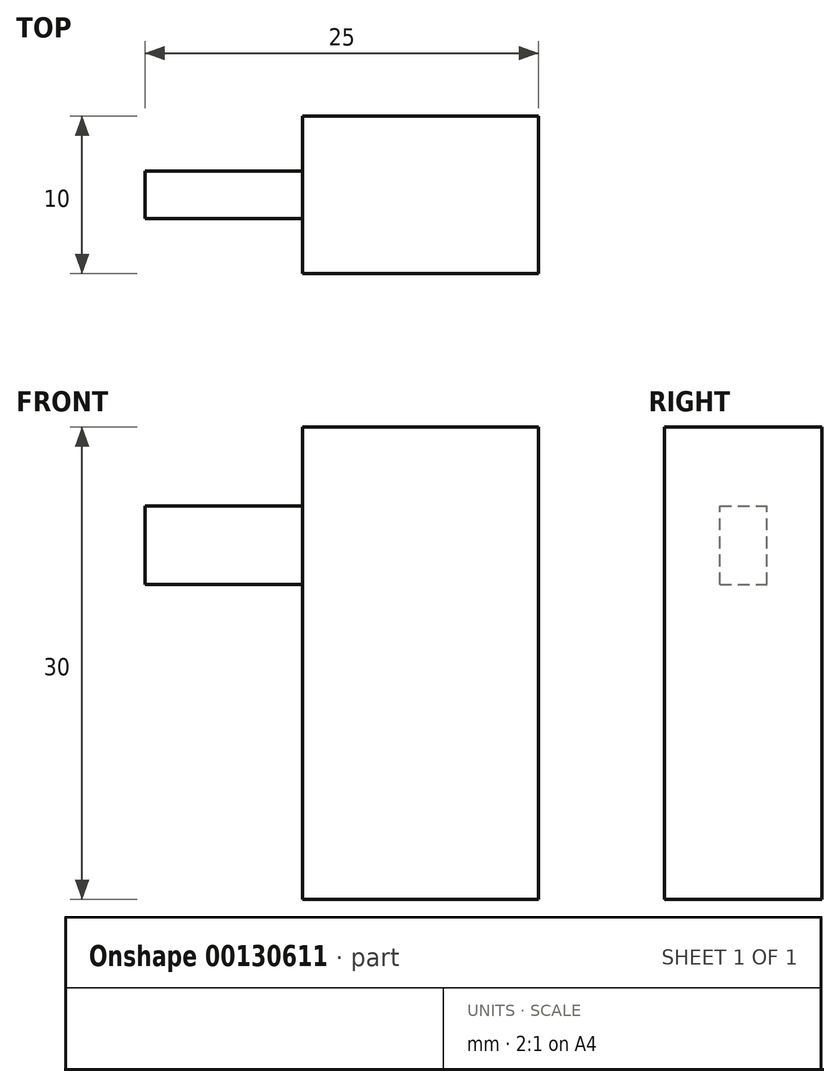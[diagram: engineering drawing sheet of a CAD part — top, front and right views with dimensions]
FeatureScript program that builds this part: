
annotation { "Feature Type Name" : "Feature", "Feature Type Description" : "" }
export const myFeature = defineFeature(function(context is Context, id is Id, definition is map)
    precondition{}
    {
        {
            var Q0;
            Q0=qCreatedBy(makeId("Front.planeOp"),FACE);
            var sketch = newSketch(context, id + "F0", { "sketchPlane" : qUnion([Q0])});
            skLineSegment(sketch, "E0.bottom", {"start": v(7.5, 15) * mm, "end": v(-7.5, 15) * mm});
            skLineSegment(sketch, "E0.top", {"start": v(7.5, -15) * mm, "end": v(-7.5, -15) * mm});
            skLineSegment(sketch, "E0.left", {"start": v(7.5, 15) * mm, "end": v(7.5, -15) * mm});
            skLineSegment(sketch, "E0.right", {"start": v(-7.5, 15) * mm, "end": v(-7.5, -15) * mm});
            skPoint(sketch, "E0.middle", {"position": v(0, 0) * mm});
            skSolve(sketch);
        }
        {
            var Q0;
            Q0=makeQuery(id+"F0.imprint","IMPRINT",FACE,{"disambiguationData":[TD([[makeQuery(id+"F0.imprint","IMPRINT",EDGE,{"derivedFrom":sQuery(id+"F0.wireOp",EDGE,"E0.bottom")}),1.0]])]});
            extrude(context, id + "F1", {"entities" : qUnion([Q0]), "oppositeDirection" : true, "depth" : 10 * mm});
        }
        {
            var Q0;
            Q0=makeQuery(id+"F1.opExtrude","SWEPT_FACE",FACE,{"disambiguationData":[OSD([sQuery(id+"F0.wireOp",EDGE,"E0.right")])]});
            var sketch = newSketch(context, id + "F2", { "sketchPlane" : qUnion([Q0])});
            skLineSegment(sketch, "E1.bottom", {"start": v(-3.5, 5) * mm, "end": v(-6.5, 5) * mm});
            skLineSegment(sketch, "E1.top", {"start": v(-3.5, 10) * mm, "end": v(-6.5, 10) * mm});
            skLineSegment(sketch, "E1.left", {"start": v(-3.5, 5) * mm, "end": v(-3.5, 10) * mm});
            skLineSegment(sketch, "E1.right", {"start": v(-6.5, 5) * mm, "end": v(-6.5, 10) * mm});
            skPoint(sketch, "E1.middle", {"position": v(-5, 7.5) * mm});
            skPoint(sketch, "E1.middle.positionSnap0", {"position": v(-5, 15) * mm});
            skPoint(sketch, "E1.centerSnap0", {"position": v(-5, 15) * mm});
            skSolve(sketch);
        }
        {
            var Q0;
            Q0=makeQuery(id+"F2.imprint","IMPRINT",FACE,{"disambiguationData":[TD([[makeQuery(id+"F2.imprint","IMPRINT",EDGE,{"derivedFrom":sQuery(id+"F2.wireOp",EDGE,"E1.bottom")}),-1.0]])]});
            extrude(context, id + "F3", {"entities" : qUnion([Q0]), "operationType" : NewBodyOperationType.ADD, "depth" : 10 * mm});
        }
    });
